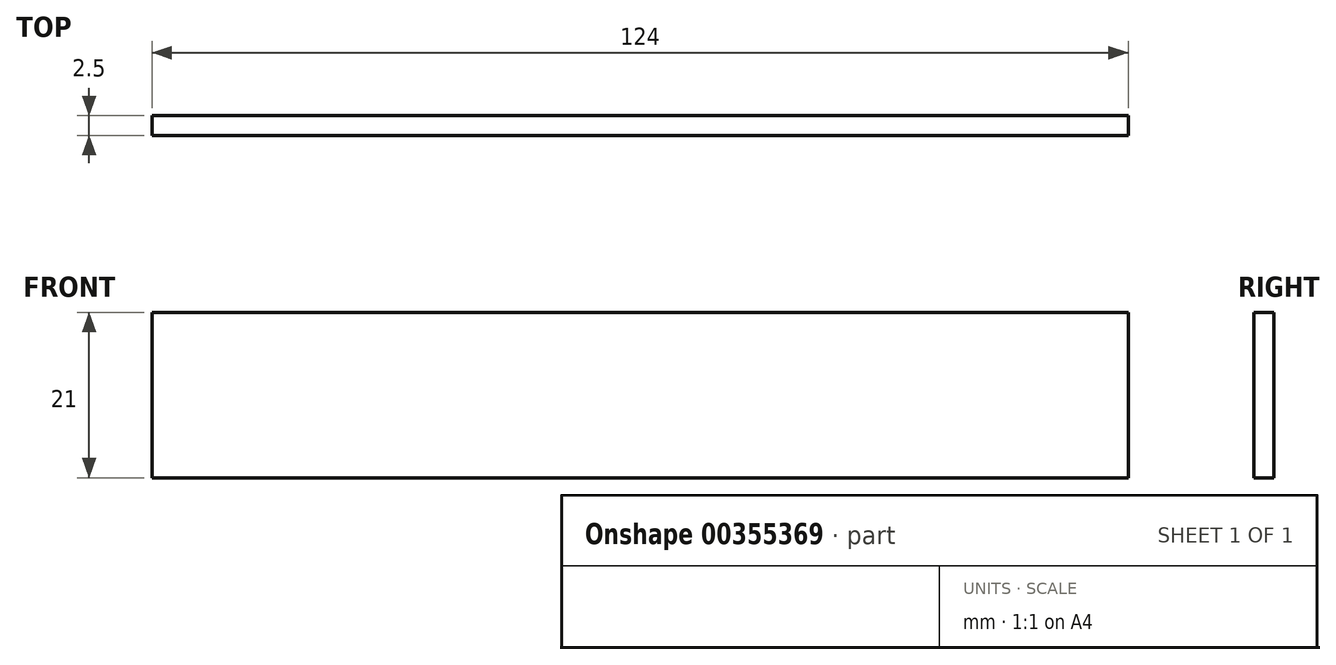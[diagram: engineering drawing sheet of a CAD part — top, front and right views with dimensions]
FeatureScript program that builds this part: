
annotation { "Feature Type Name" : "Feature", "Feature Type Description" : "" }
export const myFeature = defineFeature(function(context is Context, id is Id, definition is map)
    precondition{}
    {
        {
            var Q0;
            Q0=qCreatedBy(makeId("Front.planeOp"),FACE);
            var sketch = newSketch(context, id + "F0", { "sketchPlane" : qUnion([Q0])});
            skLineSegment(sketch, "E0.bottom", {"start": v(0, 0) * mm, "end": v(124, 0) * mm});
            skLineSegment(sketch, "E0.top", {"start": v(0, 21) * mm, "end": v(124, 21) * mm});
            skLineSegment(sketch, "E0.left", {"start": v(0, 0) * mm, "end": v(0, 21) * mm});
            skLineSegment(sketch, "E0.right", {"start": v(124, 0) * mm, "end": v(124, 21) * mm});
            skSolve(sketch);
        }
        {
            var Q0;
            Q0=qSketchRegion(id+"F0",true);
            extrude(context, id + "F1", {"entities" : qUnion([Q0]), "depth" : 2.5 * mm});
        }
    });
